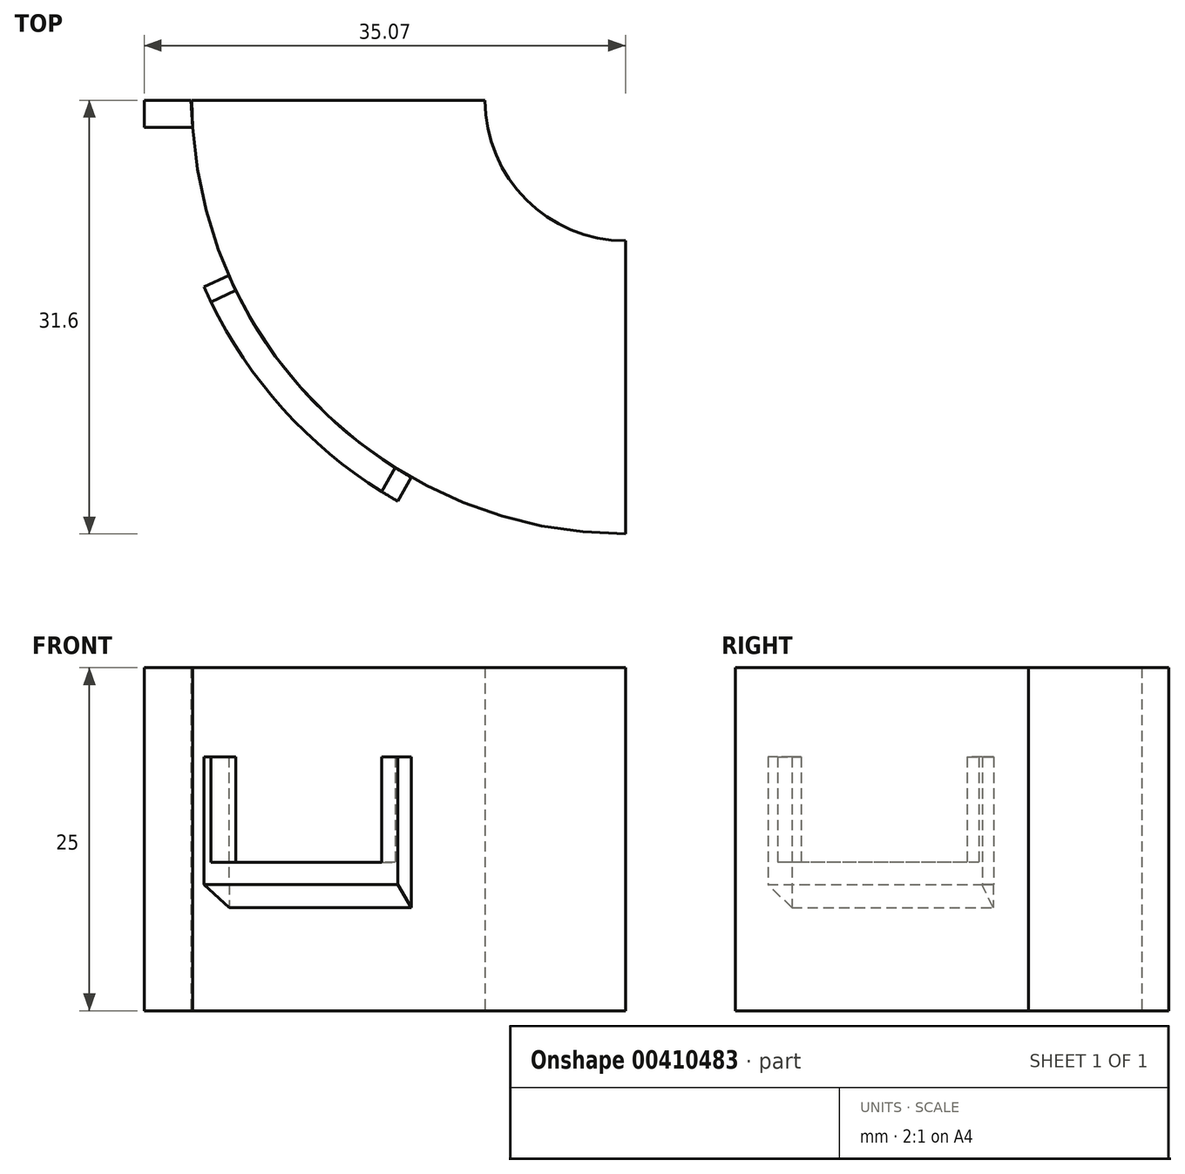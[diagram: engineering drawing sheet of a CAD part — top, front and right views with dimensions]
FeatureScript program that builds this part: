
annotation { "Feature Type Name" : "Feature", "Feature Type Description" : "" }
export const myFeature = defineFeature(function(context is Context, id is Id, definition is map)
    precondition{}
    {
        {
            var Q0;
            Q0=qCreatedBy(makeId("Top.planeOp"),FACE);
            var sketch = newSketch(context, id + "F0", { "sketchPlane" : qUnion([Q0])});
            skLineSegment(sketch, "E0", {"start": v(-42.65, 0) * mm, "end": v(43.5, 0) * mm});
            skLineSegment(sketch, "E1", {"start": v(0, 27.3) * mm, "end": v(0, -32.87) * mm});
            skCircle(sketch, "E2", {"center": v(0, 0) * mm, "radius": 10.24 * mm});
            skCircle(sketch, "E3", {"center": v(0, 0) * mm, "radius": 31.6 * mm});
            skLineSegment(sketch, "E4", {"start": v(-35.07, 0) * mm, "end": v(-35.07, -1.96) * mm});
            skLineSegment(sketch, "E5", {"start": v(-35.07, -1.96) * mm, "end": v(-31.54, -1.96) * mm});
            skLineSegment(sketch, "E6", {"start": v(-31.54, -1.96) * mm, "end": v(-31.66, 0) * mm});
            skLineSegment(sketch, "E7", {"start": v(-31.66, 0) * mm, "end": v(-35.07, 0) * mm});
            skSolve(sketch);
        }
        {
            var Q0;
            {var subQ0=sQuery(id+"F0.wireOp",EDGE,"E3");var subQ2=sQuery(id+"F0.wireOp",EDGE,"E0");var subQ3=makeQuery(id+"F0.imprint","INTERSECT",VERTEX,{"disambiguationData":[OD(1.0)],"derivedFrom":[subQ2,subQ0]});Q0=makeQuery(id+"F0.imprint","IMPRINT",FACE,{"disambiguationData":[TD([[makeQuery(id+"F0.imprint","IMPRINT",EDGE,{"disambiguationData":[TD([[subQ3,-1.0]])],"derivedFrom":subQ2}),-1.0]])]});}
            var Q1;
            Q1=makeQuery(id+"F0.imprint","IMPRINT",FACE,{"disambiguationData":[TD([[makeQuery(id+"F0.imprint","IMPRINT",EDGE,{"derivedFrom":sQuery(id+"F0.wireOp",EDGE,"E4")}),1.0]])]});
            extrude(context, id + "F1", {"entities" : qUnion([Q0, Q1]), "depth" : 25 * mm, "offsetDistance" : 25 * mm});
        }
        {
            var Q0;
            Q0=qCreatedBy(makeId("Top.planeOp"),FACE);
            var Q1;
            Q1 = qBodyType(qCreatedBy(id + "F3" ,EDGE), BodyType.WIRE);
            cPlane(context, id + "F2", {"entities" : qUnion([Q0, Q1]), "cplaneType" : CPlaneType.OFFSET, "offset" : 9.2 * mm, "width" : 150 * mm, "height" : 150 * mm});
        }
        {
            var Q0;
            Q0=qCreatedBy(id+"F2.planeOp",FACE);
            var sketch = newSketch(context, id + "F3", { "sketchPlane" : qUnion([Q0])});
            skLineSegment(sketch, "E8", {"start": v(-30.73, -13.59) * mm, "end": v(-28.9, -12.78) * mm});
            skLineSegment(sketch, "E9", {"start": v(-15.61, -27.48) * mm, "end": v(-16.6, -29.21) * mm});
            skArc(sketch, "E10", {"start": v(-30.73, -13.59) * mm, "mid": v(-24.92, -22.54) * mm, "end": v(-16.6, -29.21) * mm});
            skLineSegment(sketch, "E11", {"start": v(-30.22, -14.7) * mm, "end": v(-28.41, -13.83) * mm});
            skLineSegment(sketch, "E12", {"start": v(-17.77, -28.52) * mm, "end": v(-16.77, -26.78) * mm});
            skArc(sketch, "E13", {"start": v(-28.9, -12.78) * mm, "mid": v(-23.44, -21.2) * mm, "end": v(-15.61, -27.48) * mm});
            skSolve(sketch);
        }
        {
            var Q0;
            Q0 = qSketchRegion(id + "F3", true);
            extrude(context, id + "F4", {"entities" : qUnion([Q0]), "operationType" : NewBodyOperationType.ADD, "depth" : 1.6 * mm, "offsetDistance" : 25 * mm});
        }
        {
            var Q0;
            {var subQ0=sQuery(id+"F3.wireOp",EDGE,"E9");Q0=makeQuery(id+"F3.imprint","IMPRINT",FACE,{"disambiguationData":[TD([[makeQuery(id+"F3.imprint","IMPRINT",EDGE,{"derivedFrom":subQ0}),-1.0]])]});}
            var Q1;
            {var subQ0=sQuery(id+"F3.wireOp",EDGE,"E8");Q1=makeQuery(id+"F3.imprint","IMPRINT",FACE,{"disambiguationData":[TD([[makeQuery(id+"F3.imprint","IMPRINT",EDGE,{"derivedFrom":subQ0}),-1.0]])]});}
            extrude(context, id + "F5", {"entities" : qUnion([Q0, Q1]), "operationType" : NewBodyOperationType.ADD, "depth" : 9.3 * mm, "offsetDistance" : 25 * mm});
        }
        {
            var Q0;
            {var subQ0=sQuery(id+"F3.wireOp",EDGE,"E9");Q0=makeQuery(id+"F5.boolean.opBoolean","MERGE",FACE,{"derivedFrom":[makeQuery(id+"F4.opExtrude","SWEPT_FACE",FACE,{"disambiguationData":[OSD([subQ0])]}),makeQuery(id+"F5.opExtrude","SWEPT_FACE",FACE,{"disambiguationData":[OSD([subQ0])]})]});}
            var sketch = newSketch(context, id + "F6", { "sketchPlane" : qUnion([Q0])});
            skLineSegment(sketch, "E14", {"start": v(-33.6, 9.2) * mm, "end": v(-33.6, 9.2) * mm});
            skLineSegment(sketch, "E15", {"start": v(-33.6, 9.2) * mm, "end": v(-31.6, 9.2) * mm});
            skLineSegment(sketch, "E16", {"start": v(-31.6, 9.2) * mm, "end": v(-31.6, 7.52) * mm});
            skLineSegment(sketch, "E17", {"start": v(-31.6, 7.52) * mm, "end": v(-33.6, 9.2) * mm});
            skSolve(sketch);
        }
        {
            var Q0;
            Q0=qCreatedBy(makeId("Front.planeOp"),FACE);
            var sketch = newSketch(context, id + "F7", { "sketchPlane" : qUnion([Q0])});
            skLineSegment(sketch, "E18", {"start": v(0, 0) * mm, "end": v(0, 58.99) * mm});
            skSolve(sketch);
        }
        {
            var Q0;
            Q0=makeQuery(id+"F6.imprint","IMPRINT",FACE,{"disambiguationData":[TD([[makeQuery(id+"F6.imprint","IMPRINT",EDGE,{"derivedFrom":sQuery(id+"F6.wireOp",EDGE,"E14")}),1.0]])]});
            var Q1;
            Q1=makeQuery(id+"F6.imprint","IMPRINT",FACE,{"disambiguationData":[TD([[makeQuery(id+"F6.imprint","IMPRINT",EDGE,{"derivedFrom":sQuery(id+"F6.wireOp",EDGE,"E15")}),1.0]])]});
            var Q2;
            Q2=sQuery(id+"F7.wireOp",EDGE,"E18");
            revolve(context, id + "F8", {"operationType" : NewBodyOperationType.ADD, "entities" : qUnion([Q0, Q1]), "axis" : qUnion([Q2]), "revolveType" : RevolveType.TWO_DIRECTIONS, "angle" : 360 * degree, "angleBack" : 323.5 * degree});
        }
    });
